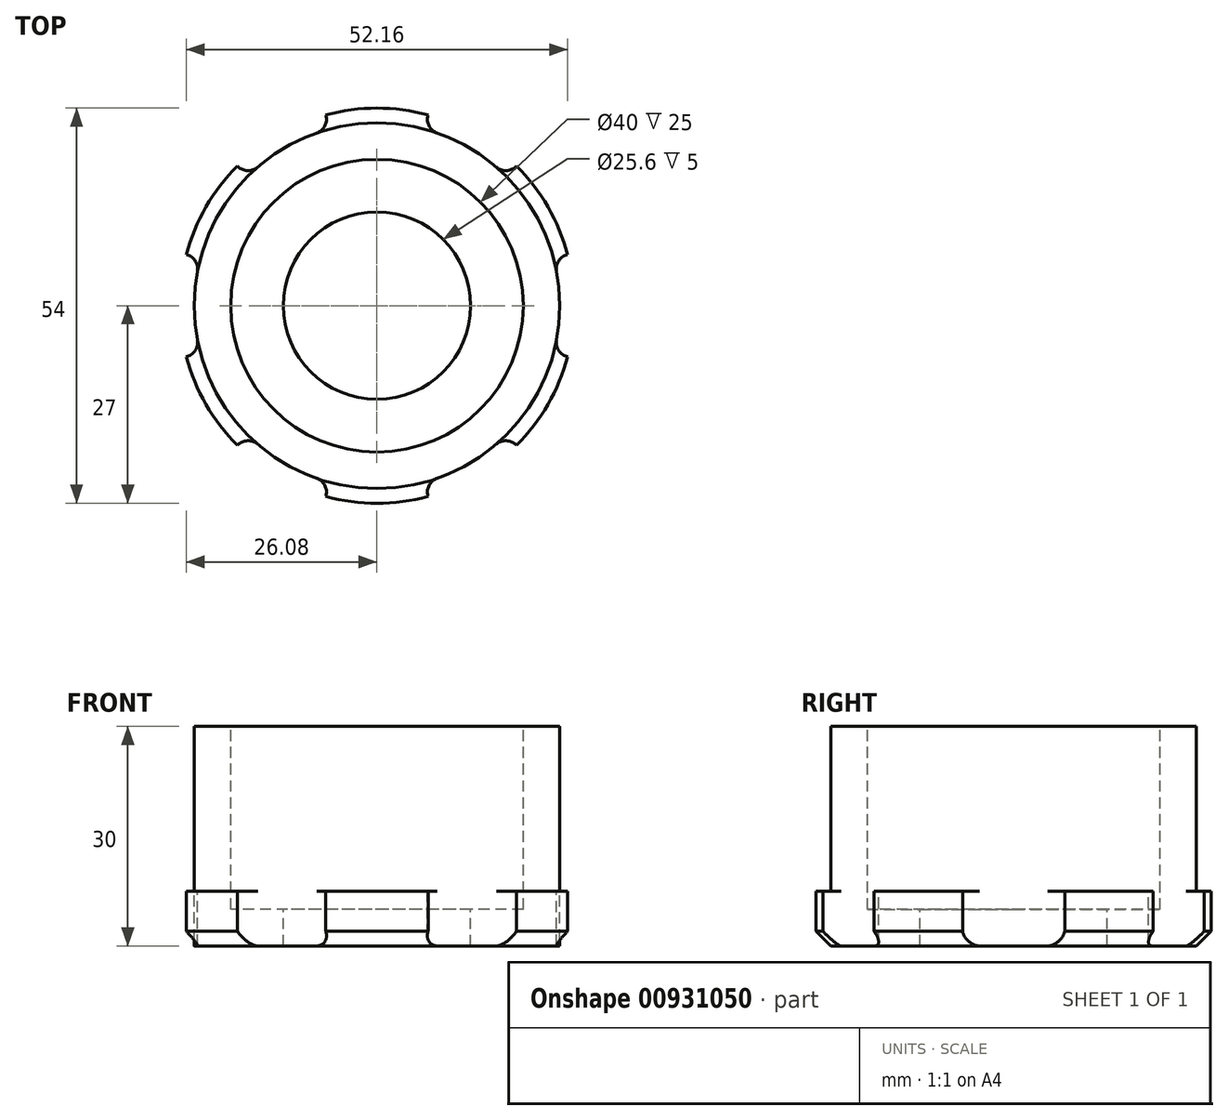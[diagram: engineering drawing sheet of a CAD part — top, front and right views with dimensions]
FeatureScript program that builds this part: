
annotation { "Feature Type Name" : "Feature", "Feature Type Description" : "" }
export const myFeature = defineFeature(function(context is Context, id is Id, definition is map)
    precondition{}
    {
        {
            var Q0;
            Q0=qCreatedBy(makeId("Right.planeOp"),FACE);
            var sketch = newSketch(context, id + "F0", { "sketchPlane" : qUnion([Q0])});
            skLineSegment(sketch, "E0", {"start": v(0, 0) * mm, "end": v(0, -50.75) * mm, "construction": true});
            skLineSegment(sketch, "E1", {"start": v(-20, 0) * mm, "end": v(-20, -25) * mm});
            skLineSegment(sketch, "E2", {"start": v(-20, 0) * mm, "end": v(-25, 0) * mm});
            skLineSegment(sketch, "E3", {"start": v(-25, 0) * mm, "end": v(-25, -22.5) * mm});
            skLineSegment(sketch, "E4", {"start": v(-25, -22.5) * mm, "end": v(-27, -22.5) * mm});
            skLineSegment(sketch, "E5", {"start": v(-27, -22.5) * mm, "end": v(-27, -30) * mm});
            skLineSegment(sketch, "E6", {"start": v(-27, -30) * mm, "end": v(-12.8, -30) * mm});
            skLineSegment(sketch, "E7", {"start": v(-12.8, -30) * mm, "end": v(-12.8, -25) * mm});
            skLineSegment(sketch, "E8", {"start": v(-12.8, -25) * mm, "end": v(-20, -25) * mm});
            skSolve(sketch);
        }
        {
            var Q0;
            Q0=makeQuery(id+"F0.imprint","IMPRINT",FACE,{"disambiguationData":[TD([[makeQuery(id+"F0.imprint","IMPRINT",EDGE,{"derivedFrom":sQuery(id+"F0.wireOp",EDGE,"E1")}),-1.0]])]});
            var Q1;
            Q1=sQuery(id+"F0.wireOp",EDGE,"E0");
            revolve(context, id + "F1", {"surfaceOperationType" : NewSurfaceOperationType.NEW, "entities" : qUnion([Q0]), "axis" : qUnion([Q1]), "revolveType" : RevolveType.FULL});
        }
        {
            var Q0;
            Q0=makeQuery(id+"F1.opRevolve","SWEPT_FACE",FACE,{"disambiguationData":[OSD([sQuery(id+"F0.wireOp",EDGE,"E6")])]});
            var sketch = newSketch(context, id + "F2", { "sketchPlane" : qUnion([Q0])});
            skArc(sketch, "E9", {"start": v(-24.15, -6.47) * mm, "mid": v(-25, 0) * mm, "end": v(-24.15, 6.47) * mm});
            skLineSegment(sketch, "E10", {"start": v(-24.15, 6.47) * mm, "end": v(-26.08, 6.99) * mm});
            skLineSegment(sketch, "E11", {"start": v(-24.15, -6.47) * mm, "end": v(-26.08, -6.99) * mm});
            skArc(sketch, "E12", {"start": v(-26.08, 6.99) * mm, "mid": v(-27, 0) * mm, "end": v(-26.08, -6.99) * mm});
            skLineSegment(sketch, "E13.1.0", {"start": v(-17.68, -17.68) * mm, "end": v(-19.1, -19.1) * mm});
            skArc(sketch, "E13.1.1", {"start": v(-6.47, -24.15) * mm, "mid": v(-12.5, -21.65) * mm, "end": v(-17.68, -17.68) * mm});
            skArc(sketch, "E13.1.2", {"start": v(-19.1, -19.1) * mm, "mid": v(-13.5, -23.38) * mm, "end": v(-6.99, -26.08) * mm});
            skLineSegment(sketch, "E13.1.3", {"start": v(-6.47, -24.15) * mm, "end": v(-6.99, -26.08) * mm});
            skLineSegment(sketch, "E13.2.0", {"start": v(6.47, -24.15) * mm, "end": v(6.99, -26.08) * mm});
            skArc(sketch, "E13.2.1", {"start": v(17.68, -17.68) * mm, "mid": v(12.5, -21.65) * mm, "end": v(6.47, -24.15) * mm});
            skArc(sketch, "E13.2.2", {"start": v(6.99, -26.08) * mm, "mid": v(13.5, -23.38) * mm, "end": v(19.1, -19.1) * mm});
            skLineSegment(sketch, "E13.2.3", {"start": v(17.68, -17.68) * mm, "end": v(19.1, -19.1) * mm});
            skLineSegment(sketch, "E13.3.0", {"start": v(24.15, -6.47) * mm, "end": v(26.08, -6.99) * mm});
            skArc(sketch, "E13.3.1", {"start": v(24.15, 6.47) * mm, "mid": v(25, 0) * mm, "end": v(24.15, -6.47) * mm});
            skArc(sketch, "E13.3.2", {"start": v(26.08, -6.99) * mm, "mid": v(27, 0) * mm, "end": v(26.08, 6.99) * mm});
            skLineSegment(sketch, "E13.3.3", {"start": v(24.15, 6.47) * mm, "end": v(26.08, 6.99) * mm});
            skLineSegment(sketch, "E13.4.0", {"start": v(17.68, 17.68) * mm, "end": v(19.1, 19.1) * mm});
            skArc(sketch, "E13.4.1", {"start": v(6.47, 24.15) * mm, "mid": v(12.5, 21.65) * mm, "end": v(17.68, 17.68) * mm});
            skArc(sketch, "E13.4.2", {"start": v(19.1, 19.1) * mm, "mid": v(13.5, 23.38) * mm, "end": v(6.99, 26.08) * mm});
            skLineSegment(sketch, "E13.4.3", {"start": v(6.47, 24.15) * mm, "end": v(6.99, 26.08) * mm});
            skLineSegment(sketch, "E13.5.0", {"start": v(-6.47, 24.15) * mm, "end": v(-6.99, 26.08) * mm});
            skArc(sketch, "E13.5.1", {"start": v(-17.68, 17.68) * mm, "mid": v(-12.5, 21.65) * mm, "end": v(-6.47, 24.15) * mm});
            skArc(sketch, "E13.5.2", {"start": v(-6.99, 26.08) * mm, "mid": v(-13.5, 23.38) * mm, "end": v(-19.1, 19.1) * mm});
            skLineSegment(sketch, "E13.5.3", {"start": v(-17.68, 17.68) * mm, "end": v(-19.1, 19.1) * mm});
            skSolve(sketch);
        }
        {
            var Q0;
            Q0 = qSketchRegion(id + "F2", true);
            extrude(context, id + "F3", {"entities" : qUnion([Q0]), "operationType" : NewBodyOperationType.REMOVE, "oppositeDirection" : true, "depth" : 25 * mm, "offsetDistance" : 25 * mm});
        }
        {
            var Q0;
            Q0=makeQuery(id+"F3.boolean.opBoolean","COPY",EDGE,{"derivedFrom":makeQuery(id+"F3.opExtrude","SWEPT_EDGE",EDGE,{"disambiguationData":[OSD([sQuery(id+"F2.wireOp",EDGE,"E13.3.0"),sQuery(id+"F2.wireOp",EDGE,"E13.3.1")])]})});
            var Q1;
            Q1=makeQuery(id+"F3.boolean.opBoolean","COPY",EDGE,{"derivedFrom":makeQuery(id+"F3.opExtrude","SWEPT_EDGE",EDGE,{"disambiguationData":[OSD([sQuery(id+"F2.wireOp",EDGE,"E13.3.1"),sQuery(id+"F2.wireOp",EDGE,"E13.3.3")])]})});
            var Q2;
            Q2=makeQuery(id+"F3.boolean.opBoolean","COPY",EDGE,{"derivedFrom":makeQuery(id+"F3.opExtrude","SWEPT_EDGE",EDGE,{"disambiguationData":[OSD([sQuery(id+"F2.wireOp",EDGE,"E13.4.0"),sQuery(id+"F2.wireOp",EDGE,"E13.4.1")])]})});
            var Q3;
            Q3=makeQuery(id+"F3.boolean.opBoolean","COPY",EDGE,{"derivedFrom":makeQuery(id+"F3.opExtrude","SWEPT_EDGE",EDGE,{"disambiguationData":[OSD([sQuery(id+"F2.wireOp",EDGE,"E13.4.1"),sQuery(id+"F2.wireOp",EDGE,"E13.4.3")])]})});
            var Q4;
            Q4=makeQuery(id+"F3.boolean.opBoolean","COPY",EDGE,{"derivedFrom":makeQuery(id+"F3.opExtrude","SWEPT_EDGE",EDGE,{"disambiguationData":[OSD([sQuery(id+"F2.wireOp",EDGE,"E13.5.0"),sQuery(id+"F2.wireOp",EDGE,"E13.5.1")])]})});
            var Q5;
            Q5=makeQuery(id+"F3.boolean.opBoolean","COPY",EDGE,{"derivedFrom":makeQuery(id+"F3.opExtrude","SWEPT_EDGE",EDGE,{"disambiguationData":[OSD([sQuery(id+"F2.wireOp",EDGE,"E9"),sQuery(id+"F2.wireOp",EDGE,"E11")])]})});
            var Q6;
            Q6=makeQuery(id+"F3.boolean.opBoolean","COPY",EDGE,{"derivedFrom":makeQuery(id+"F3.opExtrude","SWEPT_EDGE",EDGE,{"disambiguationData":[OSD([sQuery(id+"F2.wireOp",EDGE,"E13.5.1"),sQuery(id+"F2.wireOp",EDGE,"E13.5.3")])]})});
            var Q7;
            Q7=makeQuery(id+"F3.boolean.opBoolean","COPY",EDGE,{"derivedFrom":makeQuery(id+"F3.opExtrude","SWEPT_EDGE",EDGE,{"disambiguationData":[OSD([sQuery(id+"F2.wireOp",EDGE,"E9"),sQuery(id+"F2.wireOp",EDGE,"E10")])]})});
            var Q8;
            Q8=makeQuery(id+"F3.boolean.opBoolean","COPY",EDGE,{"derivedFrom":makeQuery(id+"F3.opExtrude","SWEPT_EDGE",EDGE,{"disambiguationData":[OSD([sQuery(id+"F2.wireOp",EDGE,"E13.1.0"),sQuery(id+"F2.wireOp",EDGE,"E13.1.1")])]})});
            var Q9;
            Q9=makeQuery(id+"F3.boolean.opBoolean","COPY",EDGE,{"derivedFrom":makeQuery(id+"F3.opExtrude","SWEPT_EDGE",EDGE,{"disambiguationData":[OSD([sQuery(id+"F2.wireOp",EDGE,"E13.1.1"),sQuery(id+"F2.wireOp",EDGE,"E13.1.3")])]})});
            var Q10;
            Q10=makeQuery(id+"F3.boolean.opBoolean","COPY",EDGE,{"derivedFrom":makeQuery(id+"F3.opExtrude","SWEPT_EDGE",EDGE,{"disambiguationData":[OSD([sQuery(id+"F2.wireOp",EDGE,"E13.2.0"),sQuery(id+"F2.wireOp",EDGE,"E13.2.1")])]})});
            var Q11;
            Q11=makeQuery(id+"F3.boolean.opBoolean","COPY",EDGE,{"derivedFrom":makeQuery(id+"F3.opExtrude","SWEPT_EDGE",EDGE,{"disambiguationData":[OSD([sQuery(id+"F2.wireOp",EDGE,"E13.2.1"),sQuery(id+"F2.wireOp",EDGE,"E13.2.3")])]})});
            fillet(context, id + "F4", {"entities" : qUnion([Q0, Q1, Q2, Q3, Q4, Q5, Q6, Q7, Q8, Q9, Q10, Q11]), "radius" : 2 * mm, "tangentPropagation" : true, "allowEdgeOverflow" : false});
        }
        {
            var Q0;
            {var subQ0=sQuery(id+"F0.wireOp",EDGE,"E5");var subQ1=sQuery(id+"F0.wireOp",EDGE,"E6");Q0=makeQuery(id+"F3.boolean.opBoolean","SPLIT",EDGE,{"disambiguationData":[TD([makeQuery(id+"F3.opExtrude","SWEPT_FACE",FACE,{"disambiguationData":[OSD([sQuery(id+"F2.wireOp",EDGE,"E10")])]})])],"derivedFrom":makeQuery(id+"F1.opRevolve","SWEPT_EDGE",EDGE,{"disambiguationData":[OSD([subQ0,subQ1])]})});}
            var Q1;
            {var subQ0=sQuery(id+"F0.wireOp",EDGE,"E5");var subQ1=sQuery(id+"F0.wireOp",EDGE,"E6");Q1=makeQuery(id+"F3.boolean.opBoolean","SPLIT",EDGE,{"disambiguationData":[TD([makeQuery(id+"F3.opExtrude","SWEPT_FACE",FACE,{"disambiguationData":[OSD([sQuery(id+"F2.wireOp",EDGE,"E11")])]})])],"derivedFrom":makeQuery(id+"F1.opRevolve","SWEPT_EDGE",EDGE,{"disambiguationData":[OSD([subQ0,subQ1])]})});}
            var Q2;
            {var subQ0=sQuery(id+"F0.wireOp",EDGE,"E5");var subQ1=sQuery(id+"F0.wireOp",EDGE,"E6");Q2=makeQuery(id+"F3.boolean.opBoolean","SPLIT",EDGE,{"disambiguationData":[TD([makeQuery(id+"F3.opExtrude","SWEPT_FACE",FACE,{"disambiguationData":[OSD([sQuery(id+"F2.wireOp",EDGE,"E13.1.3")])]})])],"derivedFrom":makeQuery(id+"F1.opRevolve","SWEPT_EDGE",EDGE,{"disambiguationData":[OSD([subQ0,subQ1])]})});}
            var Q3;
            {var subQ0=sQuery(id+"F0.wireOp",EDGE,"E5");var subQ1=sQuery(id+"F0.wireOp",EDGE,"E6");Q3=makeQuery(id+"F3.boolean.opBoolean","SPLIT",EDGE,{"disambiguationData":[TD([makeQuery(id+"F3.opExtrude","SWEPT_FACE",FACE,{"disambiguationData":[OSD([sQuery(id+"F2.wireOp",EDGE,"E13.2.3")])]})])],"derivedFrom":makeQuery(id+"F1.opRevolve","SWEPT_EDGE",EDGE,{"disambiguationData":[OSD([subQ0,subQ1])]})});}
            var Q4;
            {var subQ0=sQuery(id+"F0.wireOp",EDGE,"E5");var subQ1=sQuery(id+"F0.wireOp",EDGE,"E6");Q4=makeQuery(id+"F3.boolean.opBoolean","SPLIT",EDGE,{"disambiguationData":[TD([makeQuery(id+"F3.opExtrude","SWEPT_FACE",FACE,{"disambiguationData":[OSD([sQuery(id+"F2.wireOp",EDGE,"E13.3.3")])]})])],"derivedFrom":makeQuery(id+"F1.opRevolve","SWEPT_EDGE",EDGE,{"disambiguationData":[OSD([subQ0,subQ1])]})});}
            var Q5;
            {var subQ0=sQuery(id+"F0.wireOp",EDGE,"E5");var subQ1=sQuery(id+"F0.wireOp",EDGE,"E6");Q5=makeQuery(id+"F3.boolean.opBoolean","SPLIT",EDGE,{"disambiguationData":[TD([makeQuery(id+"F3.opExtrude","SWEPT_FACE",FACE,{"disambiguationData":[OSD([sQuery(id+"F2.wireOp",EDGE,"E13.4.3")])]})])],"derivedFrom":makeQuery(id+"F1.opRevolve","SWEPT_EDGE",EDGE,{"disambiguationData":[OSD([subQ0,subQ1])]})});}
            chamfer(context, id + "F5", {"entities" : qUnion([Q0, Q1, Q2, Q3, Q4, Q5]), "width" : 2 * mm, "tangentPropagation" : true});
        }
    });
